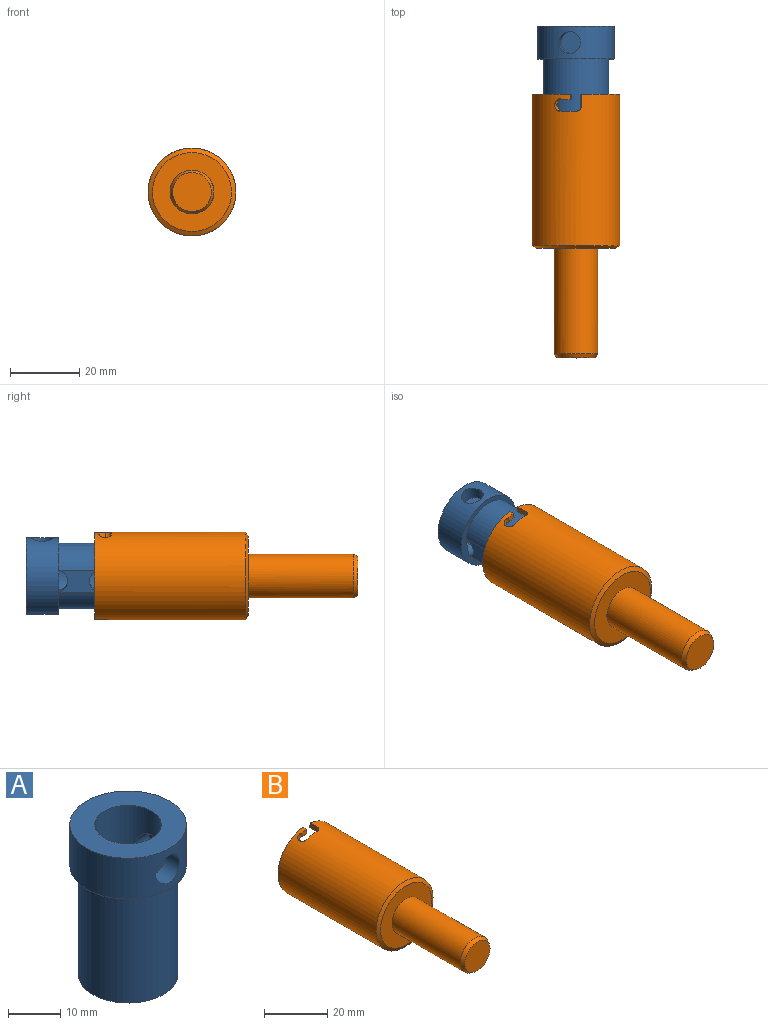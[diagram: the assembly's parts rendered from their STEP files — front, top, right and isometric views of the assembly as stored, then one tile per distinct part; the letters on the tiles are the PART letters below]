
ASSEMBLY  parts=2 mates=1
PART A: 15 faces, bbox 22.2x22.2x34.9 mm
  f0: cylinder r=11.11mm len=22.23mm, axis (0,0,-1), area 601.1mm2, adj f3,f4,f5,f13
  f1: cylinder r=9.51mm len=25.4mm, axis (0,0,-1), area 1346.4mm2, adj f2,f4,f9
  f2: plane 19.02x18.43mm, normal (0,0,-1), area 281.5mm2, adj f1,f9
  f3: plane 22.23x22.23mm, normal (0,0,1), area 261.3mm2, adj f0,f7
  f4: plane 22.23x22.23mm, normal (0,0,-1), area 106.5mm2, adj f0,f1,f9,f11
  f5: cylinder r=3.17mm len=6.35mm, axis (0,-1,0), area 74.6mm2, adj f0,f6
  f6: plane 6.35x6.35mm, normal (0,-1,0), area 31.7mm2, adj f5
  f7: cylinder r=6.35mm len=25.4mm, axis (0,0,1), area 943.9mm2, adj f3,f8,f10,f12
  f8: plane 12.7x12.7mm, normal (0,0,1), area 126.7mm2, adj f7
  f9: plane 25.4x6.6mm, normal (1,0,0), area 122.1mm2, adj f1,f2,f4,f10,f12
  f10: cylinder r=3.26mm len=6.53mm, axis (1,0,0), area 61.7mm2, adj f7,f9
  f11: plane 6.53x3.96mm, normal (-1,0,0), area 21.3mm2, adj f4,f12
  f12: cylinder r=3.26mm len=6.53mm, axis (1,0,0), area 61.7mm2, adj f7,f9,f11
  f13: cylinder r=3.17mm len=6.35mm, axis (0,1,0), area 74.6mm2, adj f0,f14
  f14: plane 6.35x6.35mm, normal (0,1,0), area 31.7mm2, adj f13
PART B: 28 faces, bbox 25.4x76.2x25.4 mm
  f0: plane 25.19x11.26mm, normal (0,1,0), area 54.5mm2, adj f1,f6,f16,f24
  f1: cylinder r=12.7mm len=43.72mm, axis (0,-1,0), area 3427.3mm2, adj f0,f5,f10,f11,f12,f13,f14,f15
  f2: plane 22.86x22.86mm, normal (0,-1,0), area 283.8mm2, adj f3,f27
  f3: cylinder r=6.35mm len=30.48mm, axis (0,1,0), area 1216.1mm2, adj f2,f26
  f4: plane 11.23x11.23mm, normal (0,-1,0), area 99.1mm2, adj f26
  f5: plane 25.19x11.26mm, normal (0,1,0), area 54.5mm2, adj f1,f6,f17,f25
  f6: cylinder r=11.11mm len=22.23mm, axis (0,-1,0), area 389.9mm2, adj f0,f5,f9,f10,f11,f12,f13,f14
  f7: plane 19.05x19.05mm, normal (0,1,0), area 285mm2, adj f8
  f8: cylinder r=9.53mm len=31.75mm, axis (0,1,0), area 1900.2mm2, adj f7,f9
  f9: plane 22.23x22.23mm, normal (0,1,0), area 102.9mm2, adj f6,f8
  f10: plane 2.31x1.98mm, normal (0,-1,0), area 3.2mm2, adj f1,f6,f11,f17
  f11: bspline ~2.86x2.53mm, area 5.4mm2, adj f1,f6,f10,f12
  f12: plane 1.39x0.76mm, normal (0.88,0,0.48), area 0.6mm2, adj f1,f6,f11,f13
  f13: bspline ~2.07x2.03mm, area 3.9mm2, adj f1,f6,f12,f14
  f14: plane 4.69x2.36mm, normal (0,1,0), area 7.1mm2, adj f1,f6,f13,f15
  f15: bspline ~1.85x1.6mm, area 3.9mm2, adj f1,f6,f14,f16
  f16: plane 3.26x1.57mm, normal (-0.99,0,0.13), area 5.2mm2, adj f0,f1,f6,f15
  f17: plane 1.57x1.57mm, normal (0.99,0,0.13), area 2.5mm2, adj f1,f5,f6,f10
  f18: bspline ~1.85x1.65mm, area 3.9mm2, adj f1,f6,f19,f25
  f19: plane 4.64x2.36mm, normal (0,1,0), area 7.1mm2, adj f1,f6,f18,f20
  f20: bspline ~2.22x2.09mm, area 3.9mm2, adj f1,f6,f19,f21
  f21: plane 1.39x0.76mm, normal (-0.88,0,-0.48), area 0.6mm2, adj f1,f6,f20,f22
  f22: bspline ~2.86x2.53mm, area 5.4mm2, adj f1,f6,f21,f23
  f23: plane 2.31x1.98mm, normal (0,-1,0), area 3.2mm2, adj f1,f6,f22,f24
  f24: plane 1.57x1.57mm, normal (-0.99,0,-0.13), area 2.5mm2, adj f0,f1,f6,f23
  f25: plane 3.26x1.57mm, normal (0.99,0,-0.13), area 5.2mm2, adj f1,f5,f6,f18
  f26: cone r=5.62mm half-angle=30deg, axis (0,1,0), area 55.1mm2, adj f3,f4
  f27: cone r=12.7mm half-angle=60deg, axis (0,1,0), area 111.2mm2, adj f1,f2
PLACE A rot(axis=(-0.06,0.71,0.71),173.1deg) t=(-22.01,18.35,-6.93)mm
PLACE B t=(-22.01,-4.63,-6.93)mm fixed
MATE cylindrical A.f0 <-> B.f1  axis (0,-1,0) through (-22.01,18.35,-6.93)mm
